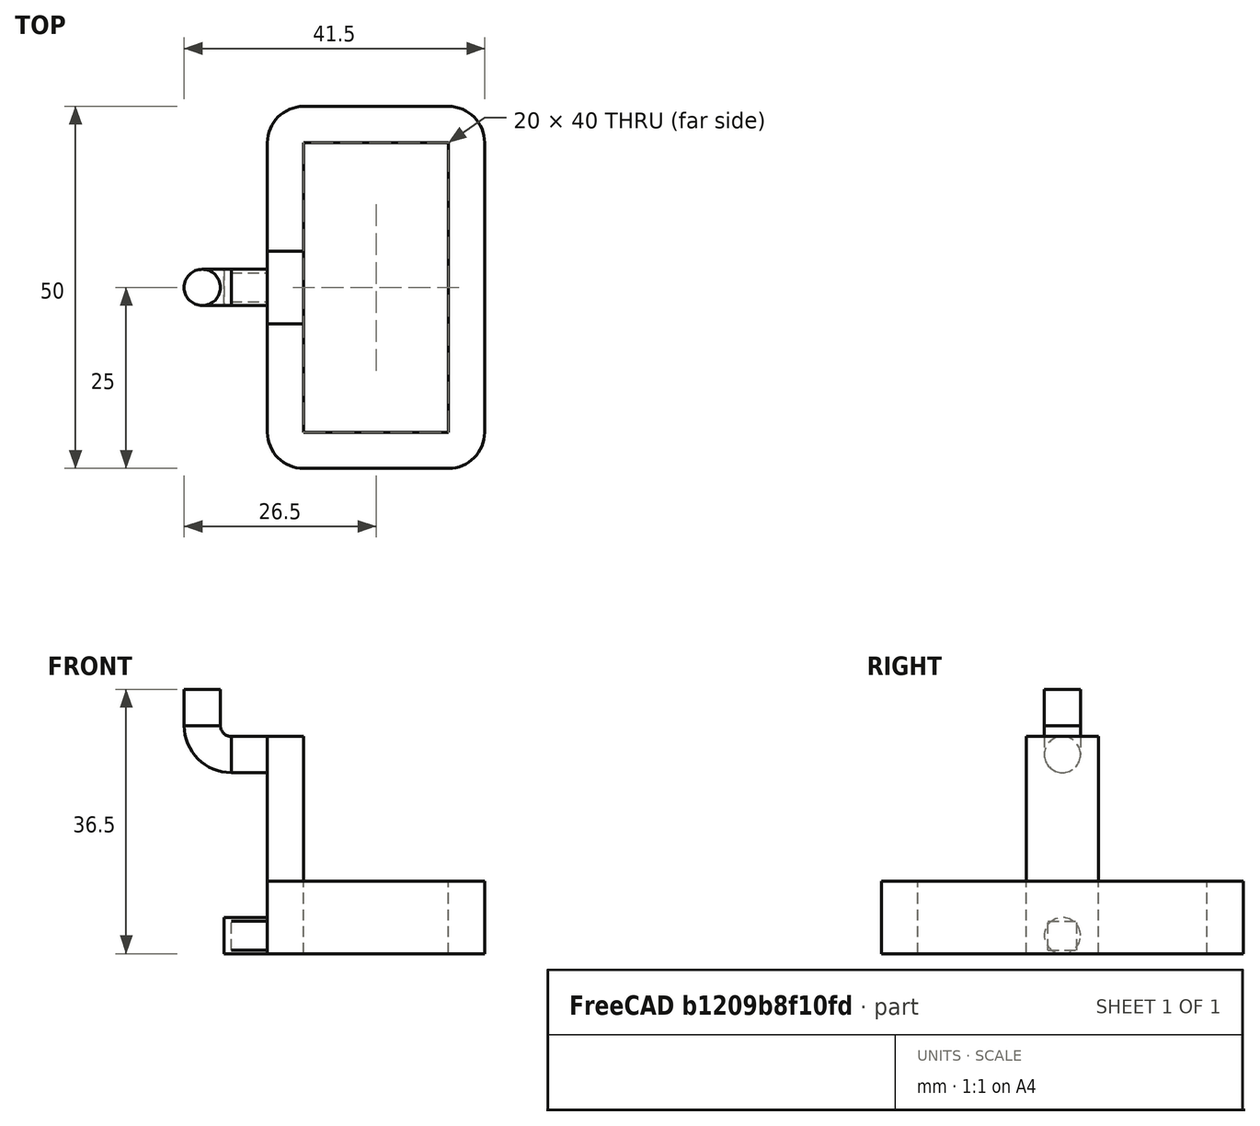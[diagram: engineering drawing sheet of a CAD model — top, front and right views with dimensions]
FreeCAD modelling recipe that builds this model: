
FCSTD DOCUMENT  (FreeCAD 0.17R13522 (Git))
Label: plier
License: All rights reserved
LicenseURL: http://en.wikipedia.org/wiki/All_rights_reserved
objects: Part::Box×4, Part::Cylinder×3, Part::Torus×1, Part::Cut×1, Part::Fillet×1
note: 10 computed .brp shape members not serialized (recipe doc carries the construction recipe); baked Part::Feature solids carry a one-line shape summary decoded from their .brp

FEATURE [Part::Cylinder] Cylinder002
  Angle = 360
  AttacherType = Attacher::AttachEngine3D
  Height = 6
  Placement = pos=(-5,0,2.5) rot=(0,-1,0;1.5708rad)
  Radius = 2.5
FEATURE [Part::Box] Box001  label="Cube001"
  AttacherType = Attacher::AttachEngine3D
  Height = 30
  Length = 5
  Placement = pos=(-5,-5,0) rot=(0,0,1;0rad)
  Width = 10
FEATURE [Part::Cylinder] Cylinder003
  Angle = 360
  AttacherType = Attacher::AttachEngine3D
  Height = 5
  Placement = pos=(-5,0,27.5) rot=(0,-1,0;1.5708rad)
  Radius = 2.5
FEATURE [Part::Torus] Torus
  Angle1 = -180
  Angle2 = 180
  Angle3 = 90
  AttacherType = Attacher::AttachEngine3D
  Placement = pos=(-10,0,31.5) rot=(0.57735,-0.57735,-0.57735;4.18879rad)
  Radius1 = 4
  Radius2 = 2.5
FEATURE [Part::Cylinder] Cylinder004
  Angle = 360
  AttacherType = Attacher::AttachEngine3D
  Height = 5
  Placement = pos=(-14,0,31.5) rot=(0,0,1;0rad)
  Radius = 2.5
FEATURE [Part::Box] Box002  label="Cube002"
  AttacherType = Attacher::AttachEngine3D
  Height = 4
  Length = 5
  Placement = pos=(-10,-2,0.5) rot=(0,0,1;0rad)
  Width = 4
FEATURE [Part::Box] Box  label="Cube"
  AttacherType = Attacher::AttachEngine3D
  Height = 10
  Length = 30
  Placement = pos=(-5,-25,0) rot=(0,0,1;0rad)
  Width = 50
FEATURE [Part::Box] Box003  label="Cube003"
  AttacherType = Attacher::AttachEngine3D
  Height = 10
  Length = 20
  Placement = pos=(0,-20,0) rot=(0,0,1;0rad)
  Width = 40
FEATURE [Part::Cut] Cut
  Base = -> Box
  Tool = -> Box003
FEATURE [Part::Fillet] Fillet
  Base = -> Cut
  Edges = 4 edges r=5: [Edge1,Edge3,Edge6,Edge15]
